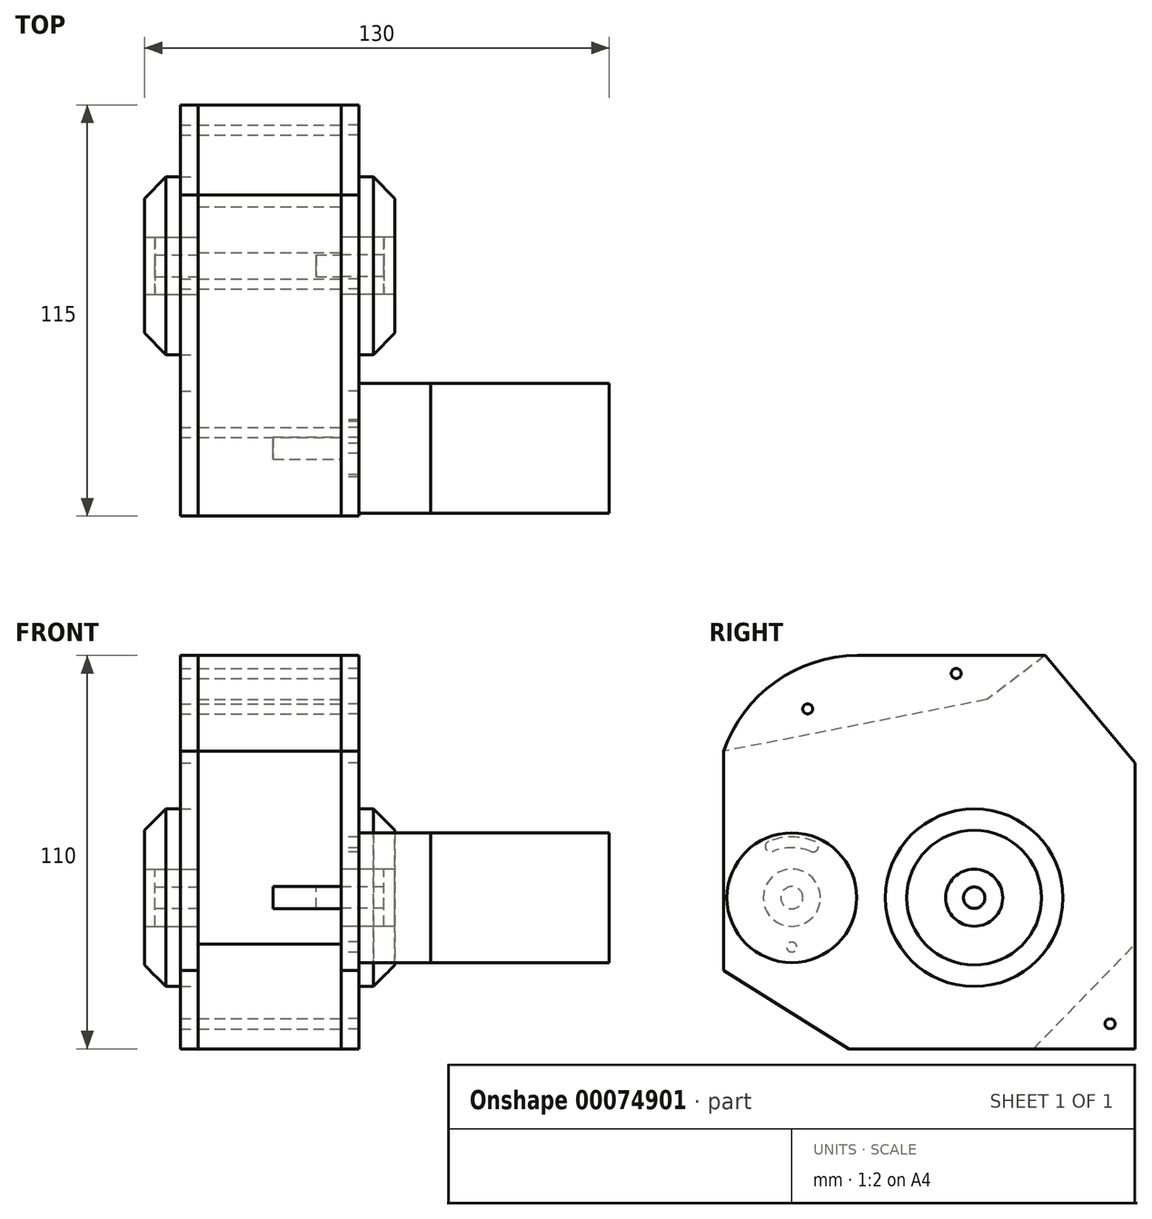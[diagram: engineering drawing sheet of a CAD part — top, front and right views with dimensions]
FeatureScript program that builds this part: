
annotation { "Feature Type Name" : "Feature", "Feature Type Description" : "" }
export const myFeature = defineFeature(function(context is Context, id is Id, definition is map)
    precondition{}
    {
        {
            var Q0;
            Q0=qCreatedBy(makeId("Right.planeOp"),FACE);
            var sketch = newSketch(context, id + "F0", { "sketchPlane" : qUnion([Q0])});
            skLineSegment(sketch, "E0.bottom", {"start": v(-32.6, 67.73) * mm, "end": v(19.8, 67.73) * mm});
            skLineSegment(sketch, "E0.top", {"start": v(-35.02, -42.27) * mm, "end": v(44.98, -42.27) * mm});
            skLineSegment(sketch, "E0.left", {"start": v(-70.02, 40.98) * mm, "end": v(-70.02, -20.4) * mm});
            skLineSegment(sketch, "E0.right", {"start": v(44.98, 37.73) * mm, "end": v(44.98, -42.27) * mm});
            skCircle(sketch, "E1", {"center": v(0, 0) * mm, "radius": 8 * mm});
            skCircle(sketch, "E2", {"center": v(0, 0) * mm, "radius": 17.84 * mm});
            skCircle(sketch, "E3", {"center": v(0, 0) * mm, "radius": 24.84 * mm});
            skCircle(sketch, "E4", {"center": v(-51, 0) * mm, "radius": 8 * mm});
            skCircle(sketch, "E5", {"center": v(-51, -13.8) * mm, "radius": 1.4 * mm});
            skArc(sketch, "E6", {"start": v(-45.64, 12.93) * mm, "mid": v(-51, 14) * mm, "end": v(-56.36, 12.93) * mm});
            skLineSegment(sketch, "E7", {"start": v(-51, 0) * mm, "end": v(-51, 14) * mm, "construction": true});
            skLineSegment(sketch, "E8", {"start": v(-45.64, 12.93) * mm, "end": v(-51, 0) * mm, "construction": true});
            skLineSegment(sketch, "E9", {"start": v(-56.36, 12.93) * mm, "end": v(-51, 0) * mm, "construction": true});
            skLineSegment(sketch, "E10", {"start": v(-56.36, 12.93) * mm, "end": v(-57.5, 15.7) * mm, "construction": true});
            skLineSegment(sketch, "E11", {"start": v(-45.64, 12.93) * mm, "end": v(-41.55, 22.8) * mm, "construction": true});
            skArc(sketch, "E12", {"start": v(-45.64, 12.93) * mm, "mid": v(-43.68, 13.75) * mm, "end": v(-44.5, 15.7) * mm});
            skArc(sketch, "E13", {"start": v(-57.5, 15.7) * mm, "mid": v(-58.32, 13.75) * mm, "end": v(-56.36, 12.93) * mm});
            skArc(sketch, "E14", {"start": v(-57.5, 15.7) * mm, "mid": v(-51, 17) * mm, "end": v(-44.5, 15.7) * mm});
            skLineSegment(sketch, "E15", {"start": v(19.8, 67.73) * mm, "end": v(44.98, 37.73) * mm});
            skLineSegment(sketch, "E16", {"start": v(-70.02, -20.4) * mm, "end": v(-35.02, -42.27) * mm});
            skArc(sketch, "E17", {"start": v(-32.6, 67.73) * mm, "mid": v(-55.6, 60.36) * mm, "end": v(-70.02, 40.98) * mm});
            skCircle(sketch, "E18", {"center": v(-46.57, 52.82) * mm, "radius": 1.4 * mm});
            skCircle(sketch, "E19", {"center": v(-5.02, 62.73) * mm, "radius": 1.4 * mm});
            skCircle(sketch, "E20", {"center": v(37.98, -35.27) * mm, "radius": 1.4 * mm});
            skLineSegment(sketch, "E21", {"start": v(19.8, 67.73) * mm, "end": v(3.63, 55.41) * mm});
            skLineSegment(sketch, "E22", {"start": v(3.63, 55.41) * mm, "end": v(-70.02, 40.98) * mm});
            skLineSegment(sketch, "E23", {"start": v(16.51, -42.27) * mm, "end": v(44.98, -13.04) * mm});
            skCircle(sketch, "E24", {"center": v(0, 0) * mm, "radius": 3 * mm});
            skCircle(sketch, "E25", {"center": v(-51, 0) * mm, "radius": 18.15 * mm});
            skCircle(sketch, "E26", {"center": v(-51, 0) * mm, "radius": 3.1 * mm});
            skSolve(sketch);
        }
        {
            var Q0;
            Q0=makeQuery(id+"F0.imprint","IMPRINT",FACE,{"disambiguationData":[TD([[makeQuery(id+"F0.imprint","IMPRINT",EDGE,{"derivedFrom":sQuery(id+"F0.wireOp",EDGE,"E0.bottom")}),-1.0]])]});
            var Q1;
            Q1=makeQuery(id+"F0.imprint","IMPRINT",FACE,{"disambiguationData":[TD([[makeQuery(id+"F0.imprint","IMPRINT",EDGE,{"derivedFrom":sQuery(id+"F0.wireOp",EDGE,"E2")}),-1.0]])]});
            var Q2;
            Q2=makeQuery(id+"F0.imprint","IMPRINT",FACE,{"disambiguationData":[TD([[makeQuery(id+"F0.imprint","IMPRINT",EDGE,{"derivedFrom":sQuery(id+"F0.wireOp",EDGE,"E1")}),-1.0]])]});
            var Q3;
            Q3=makeQuery(id+"F0.imprint","IMPRINT",FACE,{"disambiguationData":[TD([[makeQuery(id+"F0.imprint","IMPRINT",EDGE,{"derivedFrom":sQuery(id+"F0.wireOp",EDGE,"E0.left")}),1.0]])]});
            var Q4;
            Q4=makeQuery(id+"F0.imprint","IMPRINT",FACE,{"disambiguationData":[TD([[makeQuery(id+"F0.imprint","IMPRINT",EDGE,{"derivedFrom":sQuery(id+"F0.wireOp",EDGE,"E20")}),-1.0]])]});
            var Q5;
            Q5=makeQuery(id+"F0.imprint","IMPRINT",FACE,{"disambiguationData":[TD([[makeQuery(id+"F0.imprint","IMPRINT",EDGE,{"derivedFrom":sQuery(id+"F0.wireOp",EDGE,"E4")}),-1.0]])]});
            extrude(context, id + "F1", {"entities" : qUnion([Q0, Q1, Q2, Q3, Q4, Q5]), "depth" : 5 * mm});
        }
        {
            var Q0;
            Q0=makeQuery(id+"F0.imprint","IMPRINT",FACE,{"disambiguationData":[TD([[makeQuery(id+"F0.imprint","IMPRINT",EDGE,{"derivedFrom":sQuery(id+"F0.wireOp",EDGE,"E2")}),-1.0]])]});
            var Q1;
            Q1=makeQuery(id+"F0.imprint","IMPRINT",FACE,{"disambiguationData":[TD([[makeQuery(id+"F0.imprint","IMPRINT",EDGE,{"derivedFrom":sQuery(id+"F0.wireOp",EDGE,"E1")}),-1.0]])]});
            extrude(context, id + "F2", {"entities" : qUnion([Q0, Q1]), "operationType" : NewBodyOperationType.ADD, "depth" : 15 * mm});
        }
        {
            var Q0;
            Q0=makeQuery(id+"F2.opExtrude","CAP_EDGE",EDGE,{"disambiguationData":[OSD([sQuery(id+"F0.wireOp",EDGE,"E3")])],"isStart":false});
            chamfer(context, id + "F3", {"entities" : qUnion([Q0]), "width" : 6 * mm, "tangentPropagation" : true});
        }
        {
            var Q0;
            Q0=makeQuery(id+"F0.imprint","IMPRINT",FACE,{"disambiguationData":[TD([[makeQuery(id+"F0.imprint","IMPRINT",EDGE,{"derivedFrom":sQuery(id+"F0.wireOp",EDGE,"E4")}),1.0]])]});
            var Q1;
            Q1=makeQuery(id+"F0.imprint","IMPRINT",FACE,{"disambiguationData":[TD([[makeQuery(id+"F0.imprint","IMPRINT",EDGE,{"derivedFrom":sQuery(id+"F0.wireOp",EDGE,"E0.bottom")}),-1.0]])]});
            var Q2;
            Q2=makeQuery(id+"F0.imprint","IMPRINT",FACE,{"disambiguationData":[TD([[makeQuery(id+"F0.imprint","IMPRINT",EDGE,{"derivedFrom":sQuery(id+"F0.wireOp",EDGE,"E5")}),1.0]])]});
            var Q3;
            Q3=makeQuery(id+"F0.imprint","IMPRINT",FACE,{"disambiguationData":[TD([[makeQuery(id+"F0.imprint","IMPRINT",EDGE,{"derivedFrom":sQuery(id+"F0.wireOp",EDGE,"E2")}),-1.0]])]});
            var Q4;
            Q4=makeQuery(id+"F0.imprint","IMPRINT",FACE,{"disambiguationData":[TD([[makeQuery(id+"F0.imprint","IMPRINT",EDGE,{"derivedFrom":sQuery(id+"F0.wireOp",EDGE,"E1")}),-1.0]])]});
            var Q5;
            Q5=makeQuery(id+"F0.imprint","IMPRINT",FACE,{"disambiguationData":[TD([[makeQuery(id+"F0.imprint","IMPRINT",EDGE,{"derivedFrom":sQuery(id+"F0.wireOp",EDGE,"E0.left")}),1.0]])]});
            var Q6;
            Q6=makeQuery(id+"F0.imprint","IMPRINT",FACE,{"disambiguationData":[TD([[makeQuery(id+"F0.imprint","IMPRINT",EDGE,{"derivedFrom":sQuery(id+"F0.wireOp",EDGE,"E6")}),-1.0]])]});
            var Q7;
            Q7=makeQuery(id+"F0.imprint","IMPRINT",FACE,{"disambiguationData":[TD([[makeQuery(id+"F0.imprint","IMPRINT",EDGE,{"derivedFrom":sQuery(id+"F0.wireOp",EDGE,"E20")}),-1.0]])]});
            var Q8;
            Q8=makeQuery(id+"F0.imprint","IMPRINT",FACE,{"disambiguationData":[TD([[makeQuery(id+"F0.imprint","IMPRINT",EDGE,{"derivedFrom":sQuery(id+"F0.wireOp",EDGE,"E4")}),-1.0]])]});
            var Q9;
            Q9=makeQuery(id+"F0.imprint","IMPRINT",FACE,{"disambiguationData":[TD([[makeQuery(id+"F0.imprint","IMPRINT",EDGE,{"derivedFrom":sQuery(id+"F0.wireOp",EDGE,"E26")}),1.0]])]});
            extrude(context, id + "F14", {"entities" : qUnion([Q0, Q1, Q2, Q3, Q4, Q5, Q6, Q7, Q8, Q9]), "oppositeDirection" : true, "depth" : 45 * mm, "hasSecondDirection" : true, "secondDirectionOppositeDirection" : true, "secondDirectionDepth" : 40 * mm});
        }
        {
            var Q0;
            Q0=makeQuery(id+"F0.imprint","IMPRINT",FACE,{"disambiguationData":[TD([[makeQuery(id+"F0.imprint","IMPRINT",EDGE,{"derivedFrom":sQuery(id+"F0.wireOp",EDGE,"E1")}),-1.0]])]});
            var Q1;
            Q1=makeQuery(id+"F0.imprint","IMPRINT",FACE,{"disambiguationData":[TD([[makeQuery(id+"F0.imprint","IMPRINT",EDGE,{"derivedFrom":sQuery(id+"F0.wireOp",EDGE,"E2")}),-1.0]])]});
            extrude(context, id + "F4", {"entities" : qUnion([Q0, Q1]), "oppositeDirection" : true, "depth" : 55 * mm, "hasSecondDirection" : true, "secondDirectionOppositeDirection" : true, "secondDirectionDepth" : 40 * mm});
        }
        {
            var Q0;
            Q0=makeQuery(id+"F4.opExtrude","CAP_EDGE",EDGE,{"disambiguationData":[OSD([sQuery(id+"F0.wireOp",EDGE,"E3")])],"isStart":false});
            chamfer(context, id + "F5", {"entities" : qUnion([Q0]), "width" : 6 * mm, "tangentPropagation" : true});
        }
        {
            var Q0;
            Q0=makeQuery(id+"F0.imprint","IMPRINT",FACE,{"disambiguationData":[TD([[makeQuery(id+"F0.imprint","IMPRINT",EDGE,{"derivedFrom":sQuery(id+"F0.wireOp",EDGE,"E0.bottom")}),-1.0]])]});
            extrude(context, id + "F6", {"entities" : qUnion([Q0]), "oppositeDirection" : true, "depth" : 40 * mm});
        }
        {
            var Q0;
            Q0=makeQuery(id+"F0.imprint","IMPRINT",FACE,{"disambiguationData":[TD([[makeQuery(id+"F0.imprint","IMPRINT",EDGE,{"derivedFrom":sQuery(id+"F0.wireOp",EDGE,"E20")}),-1.0]])]});
            extrude(context, id + "F7", {"entities" : qUnion([Q0]), "oppositeDirection" : true, "depth" : 40 * mm});
        }
        {
            var Q0;
            Q0=makeQuery(id+"F0.imprint","IMPRINT",FACE,{"disambiguationData":[TD([[makeQuery(id+"F0.imprint","IMPRINT",EDGE,{"derivedFrom":sQuery(id+"F0.wireOp",EDGE,"E24")}),1.0]])]});
            extrude(context, id + "F8", {"entities" : qUnion([Q0]), "oppositeDirection" : true, "depth" : 7 * mm});
        }
        {
            var Q0;
            Q0=makeQuery(id+"F0.imprint","IMPRINT",FACE,{"disambiguationData":[TD([[makeQuery(id+"F0.imprint","IMPRINT",EDGE,{"derivedFrom":sQuery(id+"F0.wireOp",EDGE,"E26")}),1.0]])]});
            extrude(context, id + "F9", {"entities" : qUnion([Q0]), "oppositeDirection" : true, "depth" : 19 * mm});
        }
        {
            var Q0;
            Q0=makeQuery(id+"F0.imprint","IMPRINT",FACE,{"disambiguationData":[TD([[makeQuery(id+"F0.imprint","IMPRINT",EDGE,{"derivedFrom":sQuery(id+"F0.wireOp",EDGE,"E1")}),1.0]])]});
            extrude(context, id + "F10", {"entities" : qUnion([Q0]), "depth" : 12 * mm});
        }
        {
            var Q0;
            Q0=makeQuery(id+"F0.imprint","IMPRINT",FACE,{"disambiguationData":[TD([[makeQuery(id+"F0.imprint","IMPRINT",EDGE,{"derivedFrom":sQuery(id+"F0.wireOp",EDGE,"E1")}),1.0]])]});
            extrude(context, id + "F11", {"entities" : qUnion([Q0]), "oppositeDirection" : true, "depth" : 52 * mm, "hasSecondDirection" : true, "secondDirectionOppositeDirection" : true, "secondDirectionDepth" : 40 * mm});
        }
        {
            var Q0;
            Q0=makeQuery(id+"F0.imprint","IMPRINT",FACE,{"disambiguationData":[TD([[makeQuery(id+"F0.imprint","IMPRINT",EDGE,{"derivedFrom":sQuery(id+"F0.wireOp",EDGE,"E4")}),-1.0]])]});
            var Q1;
            Q1=makeQuery(id+"F0.imprint","IMPRINT",FACE,{"disambiguationData":[TD([[makeQuery(id+"F0.imprint","IMPRINT",EDGE,{"derivedFrom":sQuery(id+"F0.wireOp",EDGE,"E6")}),-1.0]])]});
            var Q2;
            Q2=makeQuery(id+"F0.imprint","IMPRINT",FACE,{"disambiguationData":[TD([[makeQuery(id+"F0.imprint","IMPRINT",EDGE,{"derivedFrom":sQuery(id+"F0.wireOp",EDGE,"E5")}),1.0]])]});
            var Q3;
            Q3=makeQuery(id+"F0.imprint","IMPRINT",FACE,{"disambiguationData":[TD([[makeQuery(id+"F0.imprint","IMPRINT",EDGE,{"derivedFrom":sQuery(id+"F0.wireOp",EDGE,"E4")}),1.0]])]});
            var Q4;
            Q4=makeQuery(id+"F0.imprint","IMPRINT",FACE,{"disambiguationData":[TD([[makeQuery(id+"F0.imprint","IMPRINT",EDGE,{"derivedFrom":sQuery(id+"F0.wireOp",EDGE,"E26")}),1.0]])]});
            extrude(context, id + "F12", {"entities" : qUnion([Q0, Q1, Q2, Q3, Q4]), "depth" : 25 * mm, "hasSecondDirection" : true, "secondDirectionOppositeDirection" : false, "secondDirectionDepth" : 5 * mm});
        }
        {
            var Q0;
            Q0=makeQuery(id+"F0.imprint","IMPRINT",FACE,{"disambiguationData":[TD([[makeQuery(id+"F0.imprint","IMPRINT",EDGE,{"derivedFrom":sQuery(id+"F0.wireOp",EDGE,"E4")}),-1.0]])]});
            var Q1;
            Q1=makeQuery(id+"F0.imprint","IMPRINT",FACE,{"disambiguationData":[TD([[makeQuery(id+"F0.imprint","IMPRINT",EDGE,{"derivedFrom":sQuery(id+"F0.wireOp",EDGE,"E6")}),-1.0]])]});
            var Q2;
            Q2=makeQuery(id+"F0.imprint","IMPRINT",FACE,{"disambiguationData":[TD([[makeQuery(id+"F0.imprint","IMPRINT",EDGE,{"derivedFrom":sQuery(id+"F0.wireOp",EDGE,"E4")}),1.0]])]});
            var Q3;
            Q3=makeQuery(id+"F0.imprint","IMPRINT",FACE,{"disambiguationData":[TD([[makeQuery(id+"F0.imprint","IMPRINT",EDGE,{"derivedFrom":sQuery(id+"F0.wireOp",EDGE,"E26")}),1.0]])]});
            var Q4;
            Q4=makeQuery(id+"F0.imprint","IMPRINT",FACE,{"disambiguationData":[TD([[makeQuery(id+"F0.imprint","IMPRINT",EDGE,{"derivedFrom":sQuery(id+"F0.wireOp",EDGE,"E5")}),1.0]])]});
            extrude(context, id + "F13", {"entities" : qUnion([Q0, Q1, Q2, Q3, Q4]), "depth" : 75 * mm, "hasSecondDirection" : true, "secondDirectionOppositeDirection" : false, "secondDirectionDepth" : 25 * mm});
        }
    });
